# Revit family: Urinal-Wall_Mount-KOHLER-PATIO-K-16321T
name_source: partatom
category: Plumbing Fixtures
revit_build: Autodesk Revit 2017 (Build: 20160225_1515(x64)
units: mm (PartAtom-declared; Revit-internal decimal feet)

## family parameters
Cut with Voids When Loaded = No
Host = Face
OmniClass Number = 23.31.21.00
OmniClass Title = Urinals
Part Type = Normal
Room Calculation Point = No
Round Connector Dimension = Use Diameter
Shared = No

## types (2) — shared parameters
ADA Compliant = No
Assembly Code = D2010200
CW Connection = Yes
Cold Water Inlet = Cold Water Inlet
Date Modified = 04/02/2021
Default Elevation = 0"
Finish = Kohler-Vitreous_China-0-White
Flow Rate = 0 GPM
Flush Rate- GPF = 0 GPF
Flush Rate- LPF = 0 LPF
HW Connection = No
Height = 25 1/4"
Hot Water Inlet = Hot Water Inlet
Internal Lip Height = 23 5/8"
Length = 13 3/8"
Manufacturer = KOHLER Co.
Master Format 2014 = 22 41 13.16
Master Format 2014 Name = Residential Urinals
Material = Vitreous China
Pressure = 0.00 psi
Product Documentation Link = https://files.kohler.com.cn
Product Name = PATIO
Product Page URL = https://www.kohler.com.cn
Rough-In = 17 15/16"
URL = http://www.kohler.com.cn
Vent Connection = No
Waste Connection = Yes
Waste Water Outlet = Waste Water Outlet
WaterSense Certified = No
Width = 13 1/8"

## per-type parameters (varying)
| type | Description | Model | Type |
| 1 LPF, 0-White | Water-saving automatic sensor urinal | K-16321T-M-0 | 1 |
| 0.5 LPF, 0-White | Super water-saving automatic sensor urinal | K-16321T-Y-0 | 2 |

## geometry (parser evidence)
native form markers: Sweep x5
no freeform markers — native parametric forms only
